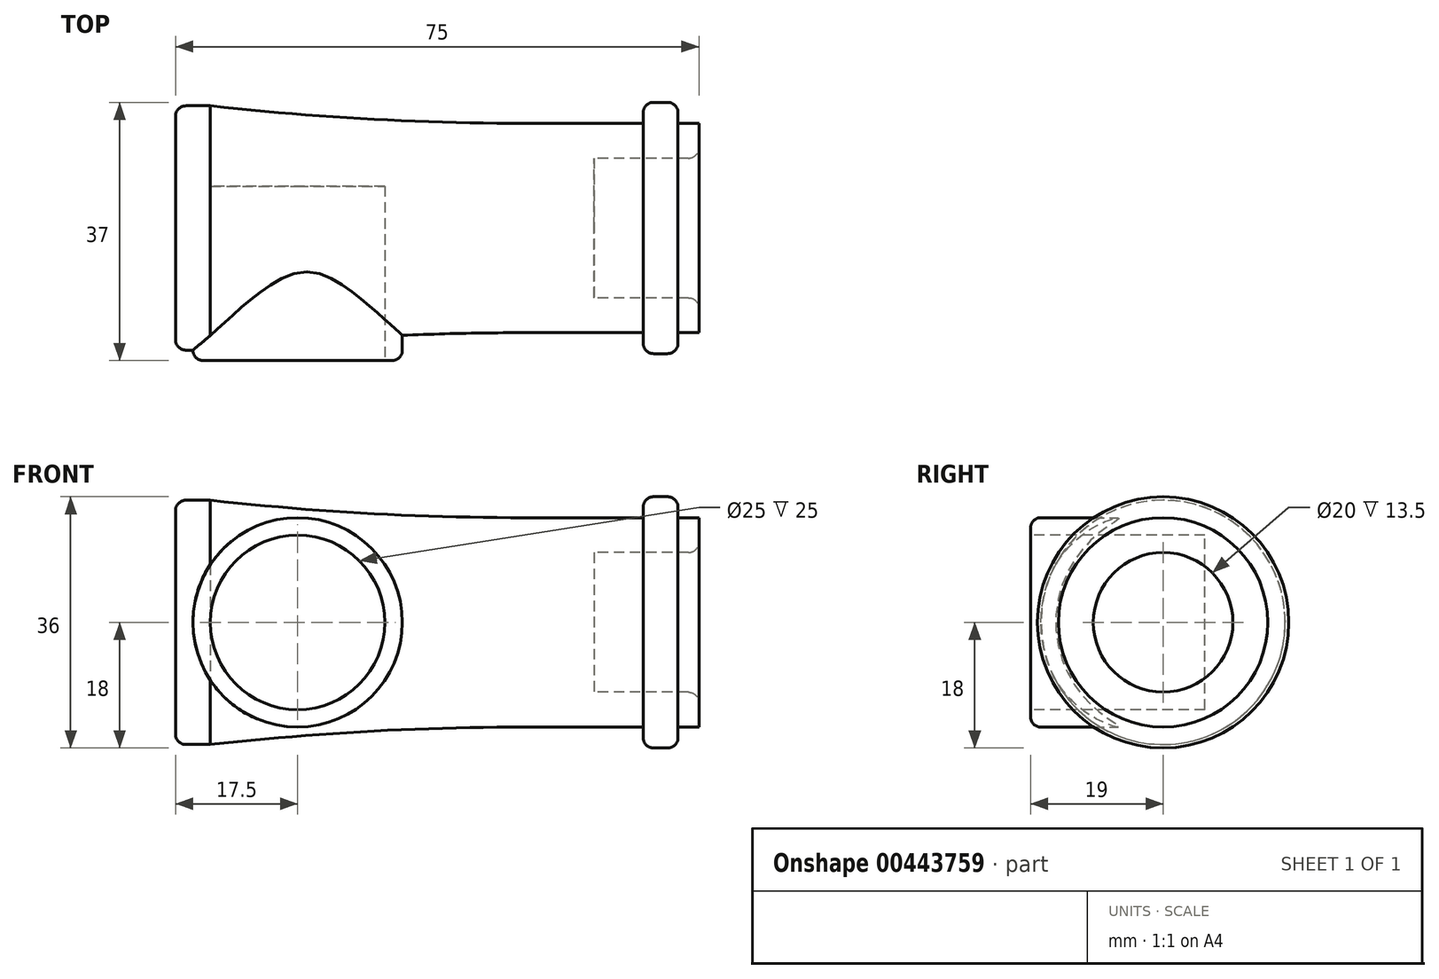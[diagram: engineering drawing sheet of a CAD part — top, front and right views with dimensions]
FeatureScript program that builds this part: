
annotation { "Feature Type Name" : "Feature", "Feature Type Description" : "" }
export const myFeature = defineFeature(function(context is Context, id is Id, definition is map)
    precondition{}
    {
        {
            var Q0;
            Q0=qCreatedBy(makeId("Front.planeOp"),FACE);
            var sketch = newSketch(context, id + "F0", { "sketchPlane" : qUnion([Q0])});
            skLineSegment(sketch, "E0", {"start": v(0, 0) * mm, "end": v(0, 17.5) * mm});
            skLineSegment(sketch, "E1", {"start": v(0, 17.5) * mm, "end": v(5, 17.5) * mm});
            skLineSegment(sketch, "E2", {"start": v(0, 0) * mm, "end": v(60, 0) * mm});
            skLineSegment(sketch, "E3", {"start": v(60, 0) * mm, "end": v(60, 10) * mm});
            skLineSegment(sketch, "E4", {"start": v(60, 10) * mm, "end": v(75, 10) * mm});
            skLineSegment(sketch, "E5", {"start": v(75, 10) * mm, "end": v(75, 15) * mm});
            skLineSegment(sketch, "E6", {"start": v(75, 15) * mm, "end": v(72, 15) * mm});
            skLineSegment(sketch, "E7", {"start": v(67, 15) * mm, "end": v(50, 15) * mm});
            skArc(sketch, "E8", {"start": v(5, 17.5) * mm, "mid": v(27.47, 15.63) * mm, "end": v(50, 15) * mm});
            skLineSegment(sketch, "E9", {"start": v(67, 15) * mm, "end": v(67, 18) * mm});
            skLineSegment(sketch, "E10", {"start": v(67, 18) * mm, "end": v(72, 18) * mm});
            skLineSegment(sketch, "E11", {"start": v(72, 18) * mm, "end": v(72, 15) * mm});
            skSolve(sketch);
        }
        {
            var Q0;
            Q0=makeQuery(id+"F0.imprint","IMPRINT",FACE,{"disambiguationData":[TD([[makeQuery(id+"F0.imprint","IMPRINT",EDGE,{"derivedFrom":sQuery(id+"F0.wireOp",EDGE,"E0")}),-1.0]])]});
            var Q1;
            Q1=sQuery(id+"F0.wireOp",EDGE,"E2");
            revolve(context, id + "F1", {"entities" : qUnion([Q0]), "axis" : qUnion([Q1]), "revolveType" : RevolveType.FULL});
        }
        {
            var Q0;
            Q0=qCreatedBy(makeId("Front.planeOp"),FACE);
            var sketch = newSketch(context, id + "F2", { "sketchPlane" : qUnion([Q0])});
            skCircle(sketch, "E12", {"center": v(17.5, 0) * mm, "radius": 15 * mm});
            skSolve(sketch);
        }
        {
            var Q0;
            Q0 = qSketchRegion(id + "F2", true);
            extrude(context, id + "F3", {"entities" : qUnion([Q0]), "operationType" : NewBodyOperationType.ADD, "depth" : 19 * mm});
        }
        {
            var Q0;
            Q0=makeQuery(id+"F3.opExtrude","CAP_FACE",FACE,{"disambiguationData":[OSD([sQuery(id+"F2.wireOp",EDGE,"E12")])],"isStart":false});
            var sketch = newSketch(context, id + "F4", { "sketchPlane" : qUnion([Q0])});
            skCircle(sketch, "E13", {"center": v(17.5, 0) * mm, "radius": 12.5 * mm});
            skSolve(sketch);
        }
        {
            var Q0;
            Q0 = qSketchRegion(id + "F4", true);
            extrude(context, id + "F5", {"entities" : qUnion([Q0]), "operationType" : NewBodyOperationType.REMOVE, "oppositeDirection" : true, "depth" : 25 * mm});
        }
        {
            var Q0;
            Q0=makeQuery(id+"F1.opRevolve","SWEPT_EDGE",EDGE,{"disambiguationData":[OSD([sQuery(id+"F0.wireOp",EDGE,"E0"),sQuery(id+"F0.wireOp",EDGE,"E1")])]});
            var Q1;
            Q1=makeQuery(id+"F3.opExtrude","CAP_EDGE",EDGE,{"disambiguationData":[OSD([sQuery(id+"F2.wireOp",EDGE,"E12")])],"isStart":false});
            var Q2;
            Q2=makeQuery(id+"F1.opRevolve","SWEPT_EDGE",EDGE,{"disambiguationData":[OSD([sQuery(id+"F0.wireOp",EDGE,"E9"),sQuery(id+"F0.wireOp",EDGE,"E10")])]});
            var Q3;
            Q3=makeQuery(id+"F1.opRevolve","SWEPT_EDGE",EDGE,{"disambiguationData":[OSD([sQuery(id+"F0.wireOp",EDGE,"E10"),sQuery(id+"F0.wireOp",EDGE,"E11")])]});
            var Q4;
            Q4=makeQuery(id+"F1.opRevolve","SWEPT_EDGE",EDGE,{"disambiguationData":[OSD([sQuery(id+"F0.wireOp",EDGE,"E4"),sQuery(id+"F0.wireOp",EDGE,"E5")])]});
            fillet(context, id + "F6", {"entities" : qUnion([Q0, Q1, Q2, Q3, Q4]), "radius" : 1.5 * mm, "tangentPropagation" : true, "allowEdgeOverflow" : false});
        }
    });
